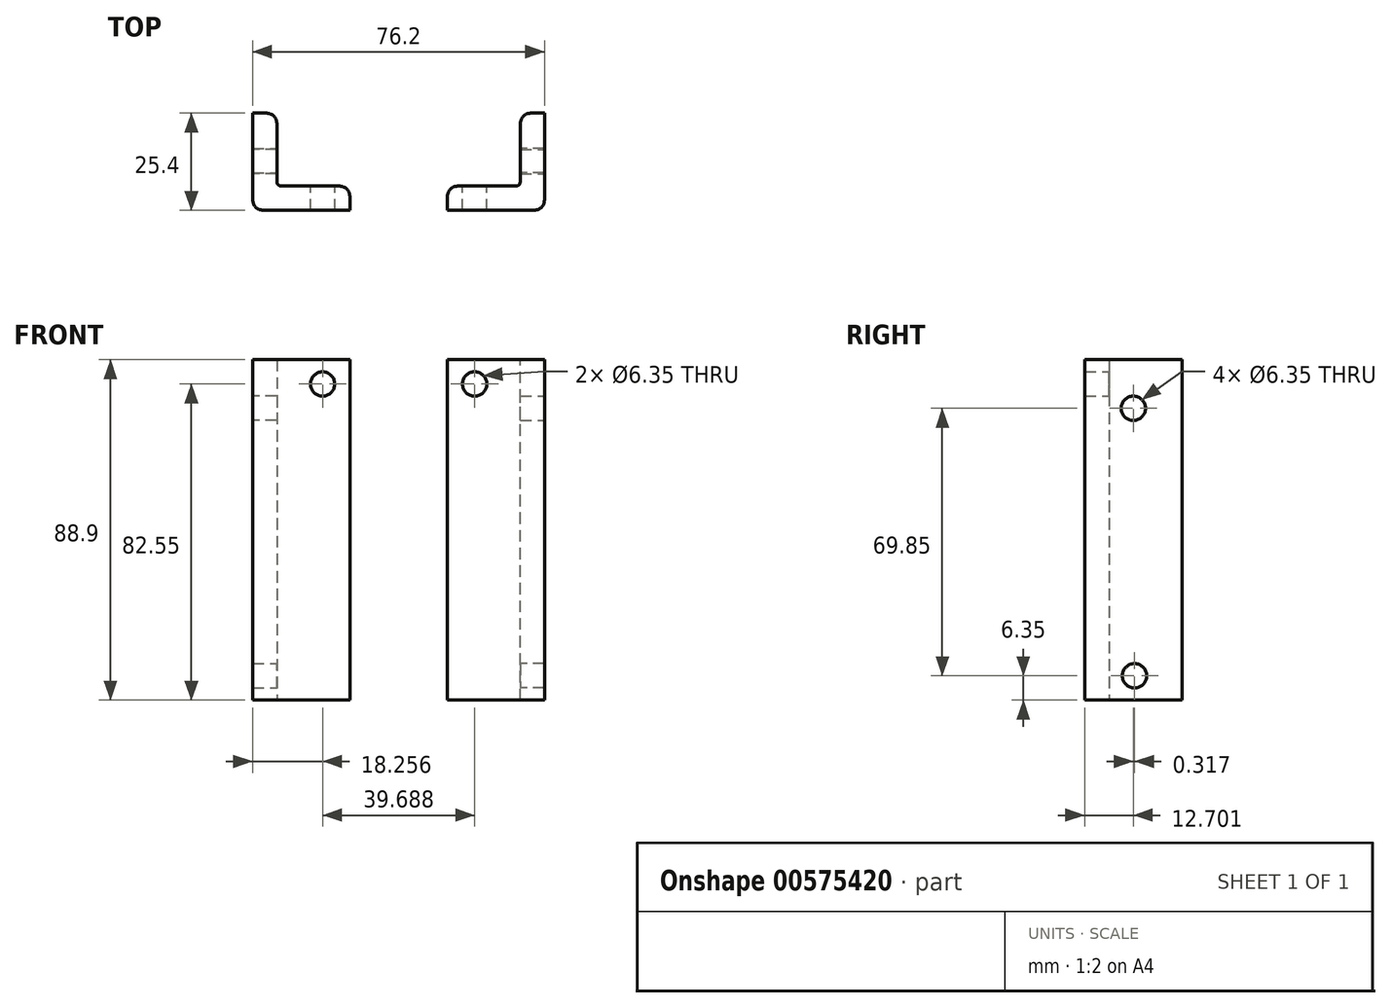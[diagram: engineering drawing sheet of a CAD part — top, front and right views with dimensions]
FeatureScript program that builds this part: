
annotation { "Feature Type Name" : "Feature", "Feature Type Description" : "" }
export const myFeature = defineFeature(function(context is Context, id is Id, definition is map)
    precondition{}
    {
        {
            var Q0;
            Q0=qCreatedBy(makeId("Top.planeOp"),FACE);
            var sketch = newSketch(context, id + "F0", { "sketchPlane" : qUnion([Q0])});
            skLineSegment(sketch, "E0", {"start": v(-19.05, 7.57) * mm, "end": v(-19.05, -11.48) * mm});
            skLineSegment(sketch, "E1", {"start": v(-19.05, -11.48) * mm, "end": v(0, -11.48) * mm});
            skLineSegment(sketch, "E2", {"start": v(0, -11.48) * mm, "end": v(0, -17.83) * mm});
            skLineSegment(sketch, "E3", {"start": v(0, -17.83) * mm, "end": v(-25.4, -17.83) * mm});
            skLineSegment(sketch, "E4", {"start": v(-25.4, -17.83) * mm, "end": v(-25.4, 7.57) * mm});
            skLineSegment(sketch, "E5", {"start": v(-25.4, 7.57) * mm, "end": v(-19.05, 7.57) * mm});
            skSolve(sketch);
        }
        {
            var Q0;
            Q0=makeQuery(id+"F0.imprint","IMPRINT",FACE,{"disambiguationData":[TD([[makeQuery(id+"F0.imprint","IMPRINT",EDGE,{"derivedFrom":sQuery(id+"F0.wireOp",EDGE,"E0")}),-1.0]])]});
            extrude(context, id + "F1", {"entities" : qUnion([Q0]), "depth" : 88.9 * mm, "offsetDistance" : 25.4 * mm});
        }
        {
            var Q0;
            Q0=makeQuery(id+"F1.opExtrude","SWEPT_EDGE",EDGE,{"disambiguationData":[OSD([sQuery(id+"F0.wireOp",EDGE,"E0"),sQuery(id+"F0.wireOp",EDGE,"E5")])]});
            var Q1;
            Q1=makeQuery(id+"F1.opExtrude","SWEPT_EDGE",EDGE,{"disambiguationData":[OSD([sQuery(id+"F0.wireOp",EDGE,"E1"),sQuery(id+"F0.wireOp",EDGE,"E2")])]});
            fillet(context, id + "F2", {"entities" : qUnion([Q0, Q1]), "radius" : 3.17 * mm, "tangentPropagation" : true, "rho" : 0.5, "crossSection" : FilletCrossSection.CONIC, "allowEdgeOverflow" : false});
        }
        {
            var Q0;
            Q0=makeQuery(id+"F1.opExtrude","SWEPT_EDGE",EDGE,{"disambiguationData":[OSD([sQuery(id+"F0.wireOp",EDGE,"E3"),sQuery(id+"F0.wireOp",EDGE,"E4")])]});
            fillet(context, id + "F3", {"entities" : qUnion([Q0]), "radius" : 3.17 * mm, "tangentPropagation" : true, "rho" : 0.5, "crossSection" : FilletCrossSection.CONIC, "allowEdgeOverflow" : false});
        }
        {
            var Q0;
            Q0=qCreatedBy(makeId("Top.planeOp"),FACE);
            var sketch = newSketch(context, id + "F4", { "sketchPlane" : qUnion([Q0])});
            skLineSegment(sketch, "E6", {"start": v(25.4, -17.83) * mm, "end": v(50.8, -17.83) * mm});
            skLineSegment(sketch, "E7", {"start": v(50.8, -17.83) * mm, "end": v(50.8, 7.57) * mm});
            skLineSegment(sketch, "E8", {"start": v(50.8, 7.57) * mm, "end": v(44.45, 7.57) * mm});
            skLineSegment(sketch, "E9", {"start": v(44.45, 7.57) * mm, "end": v(44.45, -11.48) * mm});
            skLineSegment(sketch, "E10", {"start": v(44.45, -11.48) * mm, "end": v(25.4, -11.48) * mm});
            skLineSegment(sketch, "E11", {"start": v(25.4, -11.48) * mm, "end": v(25.4, -17.83) * mm});
            skSolve(sketch);
        }
        {
            var Q0;
            Q0=makeQuery(id+"F4.imprint","IMPRINT",FACE,{"disambiguationData":[TD([[makeQuery(id+"F4.imprint","IMPRINT",EDGE,{"derivedFrom":sQuery(id+"F4.wireOp",EDGE,"E6")}),1.0]])]});
            extrude(context, id + "F5", {"entities" : qUnion([Q0]), "depth" : 88.9 * mm, "offsetDistance" : 25.4 * mm});
        }
        {
            var Q0;
            Q0=makeQuery(id+"F5.opExtrude","SWEPT_EDGE",EDGE,{"disambiguationData":[OSD([sQuery(id+"F4.wireOp",EDGE,"E10"),sQuery(id+"F4.wireOp",EDGE,"E11")])]});
            var Q1;
            Q1=makeQuery(id+"F5.opExtrude","SWEPT_EDGE",EDGE,{"disambiguationData":[OSD([sQuery(id+"F4.wireOp",EDGE,"E8"),sQuery(id+"F4.wireOp",EDGE,"E9")])]});
            fillet(context, id + "F6", {"entities" : qUnion([Q0, Q1]), "radius" : 3.17 * mm, "tangentPropagation" : true, "rho" : 0.5, "crossSection" : FilletCrossSection.CONIC, "allowEdgeOverflow" : false});
        }
        {
            var Q0;
            Q0=makeQuery(id+"F5.opExtrude","SWEPT_EDGE",EDGE,{"disambiguationData":[OSD([sQuery(id+"F4.wireOp",EDGE,"E9"),sQuery(id+"F4.wireOp",EDGE,"E10")])]});
            var Q1;
            Q1=makeQuery(id+"F1.opExtrude","SWEPT_EDGE",EDGE,{"disambiguationData":[OSD([sQuery(id+"F0.wireOp",EDGE,"E0"),sQuery(id+"F0.wireOp",EDGE,"E1")])]});
            fillet(context, id + "F7", {"entities" : qUnion([Q0, Q1]), "radius" : 1.27 * mm, "tangentPropagation" : true, "rho" : 0.5, "crossSection" : FilletCrossSection.CONIC, "allowEdgeOverflow" : false});
        }
        {
            var Q0;
            Q0=makeQuery(id+"F5.opExtrude","SWEPT_EDGE",EDGE,{"disambiguationData":[OSD([sQuery(id+"F4.wireOp",EDGE,"E6"),sQuery(id+"F4.wireOp",EDGE,"E7")])]});
            fillet(context, id + "F8", {"entities" : qUnion([Q0]), "radius" : 3.17 * mm, "tangentPropagation" : true, "rho" : 0.5, "crossSection" : FilletCrossSection.CONIC, "allowEdgeOverflow" : false});
        }
        {
            var Q0;
            Q0=makeQuery(id+"F1.opExtrude","SWEPT_FACE",FACE,{"disambiguationData":[OSD([sQuery(id+"F0.wireOp",EDGE,"E0")])]});
            var sketch = newSketch(context, id + "F9", { "sketchPlane" : qUnion([Q0])});
            skCircle(sketch, "E12", {"center": v(-4.81, 6.35) * mm, "radius": 3.18 * mm});
            skSolve(sketch);
        }
        {
            var Q0;
            Q0=makeQuery(id+"F5.opExtrude","SWEPT_FACE",FACE,{"disambiguationData":[OSD([sQuery(id+"F4.wireOp",EDGE,"E9")])]});
            var sketch = newSketch(context, id + "F10", { "sketchPlane" : qUnion([Q0])});
            skCircle(sketch, "E13", {"center": v(4.81, 6.35) * mm, "radius": 3.18 * mm});
            skSolve(sketch);
        }
        {
            var Q0;
            Q0=makeQuery(id+"F10.imprint","IMPRINT",FACE,{"disambiguationData":[TD([[makeQuery(id+"F10.imprint","IMPRINT",EDGE,{"derivedFrom":sQuery(id+"F10.wireOp",EDGE,"E13")}),1.0]])]});
            extrude(context, id + "F11", {"entities" : qUnion([Q0]), "operationType" : NewBodyOperationType.REMOVE, "oppositeDirection" : true, "depth" : 6.35 * mm, "offsetDistance" : 25.4 * mm});
        }
        {
            var Q0;
            Q0=makeQuery(id+"F9.imprint","IMPRINT",FACE,{"disambiguationData":[TD([[makeQuery(id+"F9.imprint","IMPRINT",EDGE,{"derivedFrom":sQuery(id+"F9.wireOp",EDGE,"E12")}),1.0]])]});
            extrude(context, id + "F12", {"entities" : qUnion([Q0]), "operationType" : NewBodyOperationType.REMOVE, "oppositeDirection" : true, "depth" : 6.35 * mm, "offsetDistance" : 25.4 * mm});
        }
        {
            var Q0;
            Q0=makeQuery(id+"F5.opExtrude","SWEPT_FACE",FACE,{"disambiguationData":[OSD([sQuery(id+"F4.wireOp",EDGE,"E7")])]});
            var sketch = newSketch(context, id + "F13", { "sketchPlane" : qUnion([Q0])});
            skCircle(sketch, "E14", {"center": v(-5.13, 76.2) * mm, "radius": 3.17 * mm});
            skSolve(sketch);
        }
        {
            var Q0;
            Q0=makeQuery(id+"F1.opExtrude","SWEPT_FACE",FACE,{"disambiguationData":[OSD([sQuery(id+"F0.wireOp",EDGE,"E4")])]});
            var sketch = newSketch(context, id + "F14", { "sketchPlane" : qUnion([Q0])});
            skCircle(sketch, "E15", {"center": v(5.13, 76.2) * mm, "radius": 3.18 * mm});
            skSolve(sketch);
        }
        {
            var Q0;
            Q0=makeQuery(id+"F14.imprint","IMPRINT",FACE,{"disambiguationData":[TD([[makeQuery(id+"F14.imprint","IMPRINT",EDGE,{"derivedFrom":sQuery(id+"F14.wireOp",EDGE,"E15")}),1.0]])]});
            extrude(context, id + "F15", {"entities" : qUnion([Q0]), "operationType" : NewBodyOperationType.REMOVE, "oppositeDirection" : true, "depth" : 6.35 * mm, "offsetDistance" : 25.4 * mm});
        }
        {
            var Q0;
            Q0=makeQuery(id+"F13.imprint","IMPRINT",FACE,{"disambiguationData":[TD([[makeQuery(id+"F13.imprint","IMPRINT",EDGE,{"derivedFrom":sQuery(id+"F13.wireOp",EDGE,"E14")}),1.0]])]});
            extrude(context, id + "F16", {"entities" : qUnion([Q0]), "operationType" : NewBodyOperationType.REMOVE, "oppositeDirection" : true, "depth" : 6.35 * mm, "offsetDistance" : 25.4 * mm});
        }
        {
            var Q0;
            Q0=makeQuery(id+"F5.opExtrude","SWEPT_FACE",FACE,{"disambiguationData":[OSD([sQuery(id+"F4.wireOp",EDGE,"E10")])]});
            var sketch = newSketch(context, id + "F17", { "sketchPlane" : qUnion([Q0])});
            skCircle(sketch, "E16", {"center": v(-32.54, 82.55) * mm, "radius": 3.18 * mm});
            skSolve(sketch);
        }
        {
            var Q0;
            Q0=makeQuery(id+"F1.opExtrude","SWEPT_FACE",FACE,{"disambiguationData":[OSD([sQuery(id+"F0.wireOp",EDGE,"E1")])]});
            var sketch = newSketch(context, id + "F18", { "sketchPlane" : qUnion([Q0])});
            skCircle(sketch, "E17", {"center": v(7.14, 82.55) * mm, "radius": 3.18 * mm});
            skSolve(sketch);
        }
        {
            var Q0;
            Q0=makeQuery(id+"F17.imprint","IMPRINT",FACE,{"disambiguationData":[TD([[makeQuery(id+"F17.imprint","IMPRINT",EDGE,{"derivedFrom":sQuery(id+"F17.wireOp",EDGE,"E16")}),1.0]])]});
            extrude(context, id + "F19", {"entities" : qUnion([Q0]), "operationType" : NewBodyOperationType.REMOVE, "oppositeDirection" : true, "depth" : 6.35 * mm, "offsetDistance" : 25.4 * mm});
        }
        {
            var Q0;
            Q0=makeQuery(id+"F18.imprint","IMPRINT",FACE,{"disambiguationData":[TD([[makeQuery(id+"F18.imprint","IMPRINT",EDGE,{"derivedFrom":sQuery(id+"F18.wireOp",EDGE,"E17")}),1.0]])]});
            extrude(context, id + "F20", {"entities" : qUnion([Q0]), "operationType" : NewBodyOperationType.REMOVE, "oppositeDirection" : true, "depth" : 6.35 * mm, "offsetDistance" : 25.4 * mm});
        }
    });
